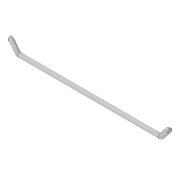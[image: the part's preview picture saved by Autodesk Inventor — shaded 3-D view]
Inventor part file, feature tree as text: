
AUTODESK INVENTOR PART (.ipt)
format: ipt  version: 2018 (Build 220112000, 112)  size: 297,984 bytes
history: native  units: in
note: dims shown in document units (in); Inventor stores cm internally (conversion verified against a paired STEP export)
features: plane x5, sketch x4, loft x1, mirror x1, extrude x1
ambient origin geometry x8: Origin, YZ Plane, XZ Plane, XY Plane, X Axis, Y Axis, Z Axis, Center Point
bodies: Body1 (feature_tree)
feature tree (12):
  sketch  "Sketch1"  dims[d0=2.5in d19=5.333in]
  plane  "Work Plane5"
  sketch  "Sketch6"  dims[d20=2.5in d21=5.333in]
  plane  "Work Plane6"
  loft  "Loft2"
  plane  "Work Plane7"
  mirror  "Mirror2"
  extrude  "Extrusion2"  Depth=5.333in
  plane  "Work Plane8"
  plane  "Work Plane9"
  sketch  "Sketch7"  dims[d22=0.0in]
  sketch  "Sketch8"  dims[d23=0.0in d24=90.0deg d25=0.0in d26=90.0deg d27=0.0in d28=90.0deg d29=-45.5in d30=1.0in d31=0.0in]
